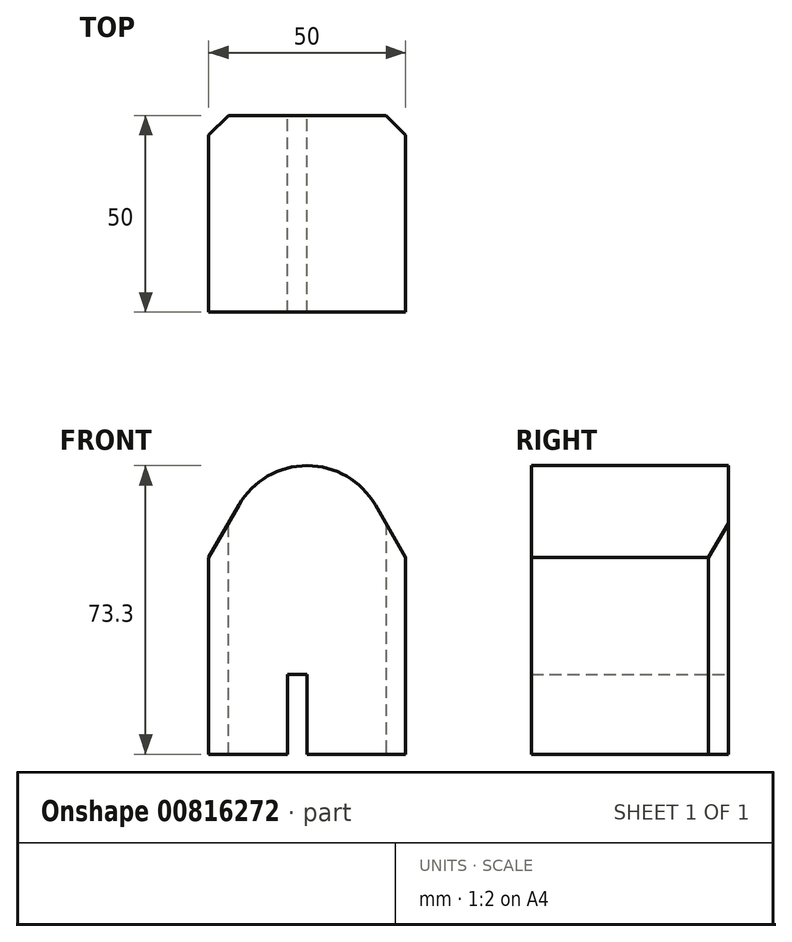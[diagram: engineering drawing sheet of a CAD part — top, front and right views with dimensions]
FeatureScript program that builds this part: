
annotation { "Feature Type Name" : "Feature", "Feature Type Description" : "" }
export const myFeature = defineFeature(function(context is Context, id is Id, definition is map)
    precondition{}
    {
        {
            var Q0;
            Q0=qCreatedBy(makeId("Front.planeOp"),FACE);
            var sketch = newSketch(context, id + "F0", { "sketchPlane" : qUnion([Q0])});
            skLineSegment(sketch, "E0.bottom", {"start": v(25, -25) * mm, "end": v(-25, -25) * mm});
            skLineSegment(sketch, "E0.left", {"start": v(25, -25) * mm, "end": v(25, 25) * mm});
            skLineSegment(sketch, "E0.right", {"start": v(-25, -25) * mm, "end": v(-25, 25) * mm});
            skPoint(sketch, "E0.middle", {"position": v(0, 0) * mm});
            skLineSegment(sketch, "E1", {"start": v(-25, 25) * mm, "end": v(0, 68.3) * mm});
            skLineSegment(sketch, "E2", {"start": v(25, 25) * mm, "end": v(0, 68.3) * mm});
            skLineSegment(sketch, "E3.bottom", {"start": v(0, -25) * mm, "end": v(-5, -25) * mm});
            skLineSegment(sketch, "E3.top", {"start": v(0, -4.77) * mm, "end": v(-5, -4.77) * mm});
            skLineSegment(sketch, "E3.left", {"start": v(0, -25) * mm, "end": v(0, -4.77) * mm});
            skLineSegment(sketch, "E3.right", {"start": v(-5, -25) * mm, "end": v(-5, -4.77) * mm});
            skSolve(sketch);
        }
        {
            var Q0;
            {var subQ1=sQuery(id+"F0.wireOp",EDGE,"E0.left");Q0=makeQuery(id+"F0.imprint","IMPRINT",FACE,{"disambiguationData":[TD([[makeQuery(id+"F0.imprint","IMPRINT",EDGE,{"derivedFrom":subQ1}),1.0]])]});}
            extrude(context, id + "F1", {"entities" : qUnion([Q0]), "depth" : 50 * mm, "offsetDistance" : 25 * mm});
        }
        {
            var Q0;
            Q0=makeQuery(id+"F1.opExtrude","SWEPT_EDGE",EDGE,{"disambiguationData":[OSD([sQuery(id+"F0.wireOp",EDGE,"E1"),sQuery(id+"F0.wireOp",EDGE,"E2")])]});
            fillet(context, id + "F2", {"entities" : qUnion([Q0]), "radius" : 20 * mm, "tangentPropagation" : true, "allowEdgeOverflow" : false});
        }
        {
            var Q0;
            Q0=makeQuery(id+"F1.opExtrude","CAP_EDGE",EDGE,{"disambiguationData":[OSD([sQuery(id+"F0.wireOp",EDGE,"E0.left")])],"isStart":true});
            var Q1;
            Q1=makeQuery(id+"F1.opExtrude","CAP_EDGE",EDGE,{"disambiguationData":[OSD([sQuery(id+"F0.wireOp",EDGE,"E0.right")])],"isStart":true});
            chamfer(context, id + "F3", {"entities" : qUnion([Q0, Q1]), "width" : 5 * mm, "tangentPropagation" : true});
        }
    });
